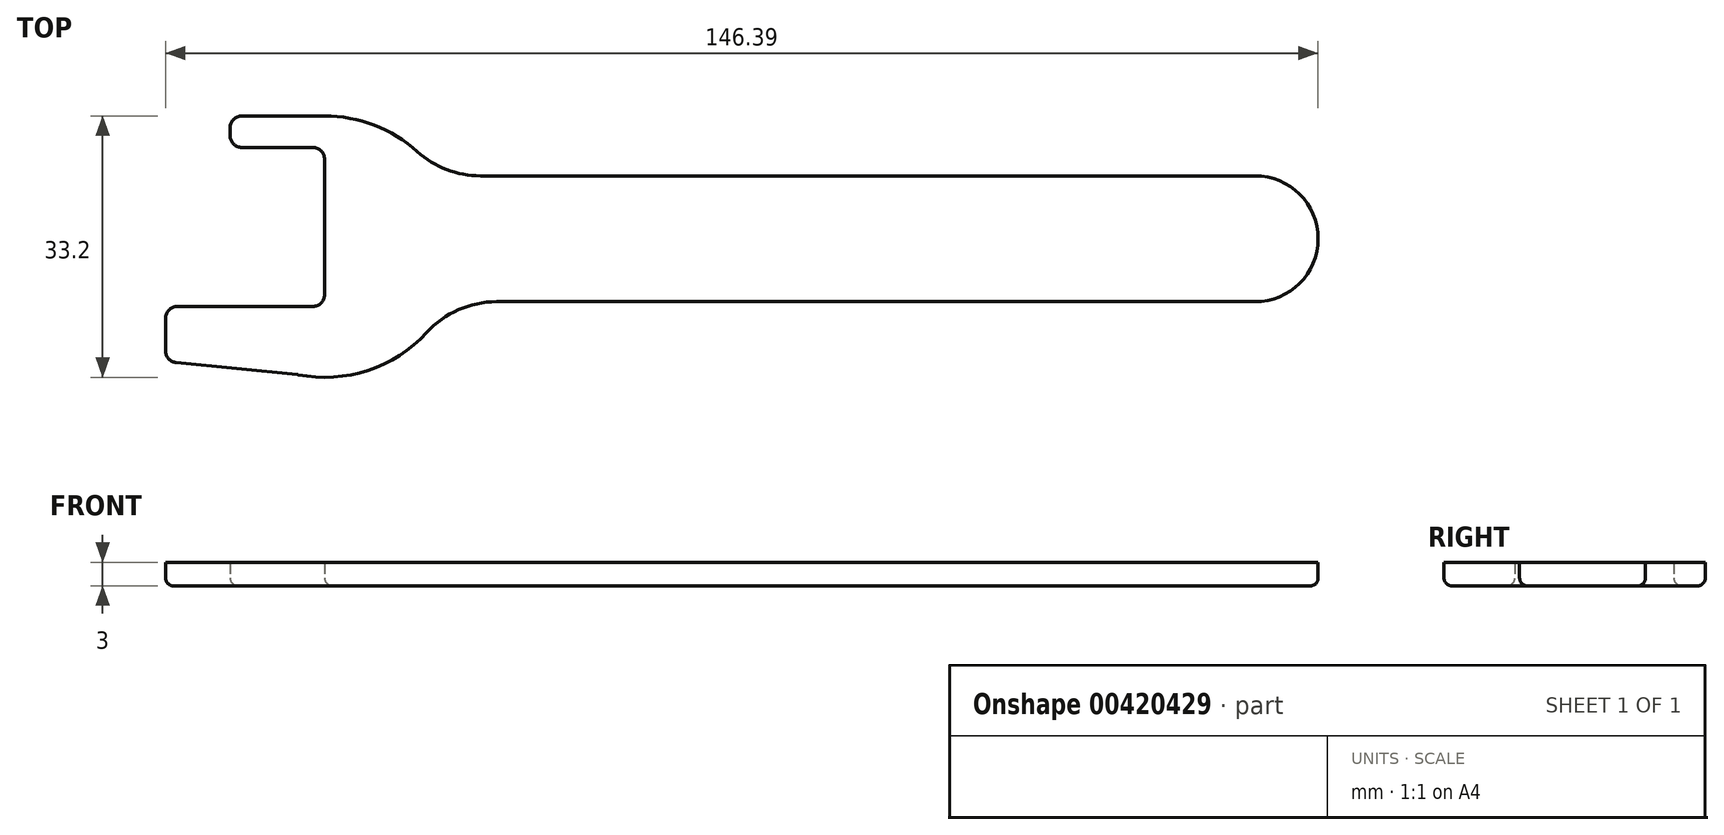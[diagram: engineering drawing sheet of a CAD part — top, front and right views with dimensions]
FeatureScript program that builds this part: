
annotation { "Feature Type Name" : "Feature", "Feature Type Description" : "" }
export const myFeature = defineFeature(function(context is Context, id is Id, definition is map)
    precondition{}
    {
        {
            var Q0;
            Q0=qCreatedBy(makeId("Top.planeOp"),FACE);
            var sketch = newSketch(context, id + "F0", { "sketchPlane" : qUnion([Q0])});
            skArc(sketch, "E0", {"start": v(-73.97, -17.26) * mm, "mid": v(-62.86, -15.84) * mm, "end": v(-54.85, -8) * mm});
            skLineSegment(sketch, "E1", {"start": v(59.4, -20.35) * mm, "end": v(59.4, 16.2) * mm, "construction": true});
            skLineSegment(sketch, "E2", {"start": v(-88.12, 35.8) * mm, "end": v(-88.12, -38.11) * mm, "construction": true});
            skLineSegment(sketch, "E3.top", {"start": v(-70.52, -17.6) * mm, "end": v(-50.32, -17.6) * mm, "construction": true});
            skLineSegment(sketch, "E3.right", {"start": v(-50.32, 17.6) * mm, "end": v(-50.32, -17.6) * mm, "construction": true});
            skLineSegment(sketch, "E4.top", {"start": v(-70.52, 11.6) * mm, "end": v(-82.52, 11.6) * mm});
            skLineSegment(sketch, "E5.top", {"start": v(-70.52, -8.6) * mm, "end": v(-90.72, -8.6) * mm});
            skLineSegment(sketch, "E5.right", {"start": v(-90.72, -15.6) * mm, "end": v(-90.72, -8.6) * mm});
            skLineSegment(sketch, "E6", {"start": v(-63.17, 15.6) * mm, "end": v(-82.52, 15.6) * mm});
            skLineSegment(sketch, "E7", {"start": v(-82.52, 15.6) * mm, "end": v(-82.52, 11.6) * mm});
            skLineSegment(sketch, "E8.trimOffspring", {"start": v(-90.72, -8.6) * mm, "end": v(-90.72, -15.6) * mm});
            skLineSegment(sketch, "E9", {"start": v(-70.52, -17.6) * mm, "end": v(-90.72, -15.6) * mm});
            skPoint(sketch, "E10.orphan", {"position": v(-90.72, -17.6) * mm});
            skLineSegment(sketch, "E11", {"start": v(-70.52, -8.6) * mm, "end": v(-70.52, 11.6) * mm});
            skLineSegment(sketch, "E12", {"start": v(-98.89, 0) * mm, "end": v(66.7, 0) * mm, "construction": true});
            skArc(sketch, "E13", {"start": v(47.67, -8) * mm, "mid": v(55.67, 0) * mm, "end": v(47.67, 8) * mm});
            skLineSegment(sketch, "E14", {"start": v(47.67, 8) * mm, "end": v(-50.32, 8) * mm});
            skLineSegment(sketch, "E15", {"start": v(47.67, -8) * mm, "end": v(-54.85, -8) * mm});
            skPoint(sketch, "E16.end.orphan", {"position": v(-61.1, 8) * mm});
            skPoint(sketch, "E17.orphan", {"position": v(-62.74, 8) * mm});
            skArc(sketch, "E18.trimOffspring", {"start": v(-56.04, 8) * mm, "mid": v(-62.35, 13.58) * mm, "end": v(-70.52, 15.6) * mm});
            skLineSegment(sketch, "E19", {"start": v(-50.32, 8) * mm, "end": v(-56.04, 8) * mm});
            skLineSegment(sketch, "E20.trimOffspring", {"start": v(-82.52, 15.6) * mm, "end": v(-46.92, 15.6) * mm, "construction": true});
            skSolve(sketch);
        }
        {
            var Q0;
            Q0=qSketchRegion(id+"F0",true);
            extrude(context, id + "F1", {"entities" : qUnion([Q0]), "depth" : 3 * mm});
        }
        {
            var Q0;
            Q0=makeQuery(id+"F1.opExtrude","SWEPT_EDGE",EDGE,{"disambiguationData":[OSD([sQuery(id+"F0.wireOp",EDGE,"E6"),sQuery(id+"F0.wireOp",EDGE,"E7")])]});
            var Q1;
            Q1=makeQuery(id+"F1.opExtrude","SWEPT_EDGE",EDGE,{"disambiguationData":[OSD([sQuery(id+"F0.wireOp",EDGE,"E4.top"),sQuery(id+"F0.wireOp",EDGE,"E7")])]});
            var Q2;
            Q2=makeQuery(id+"F1.opExtrude","SWEPT_EDGE",EDGE,{"disambiguationData":[OSD([sQuery(id+"F0.wireOp",EDGE,"E5.top"),sQuery(id+"F0.wireOp",EDGE,"E8.trimOffspring")])]});
            var Q3;
            Q3=makeQuery(id+"F1.opExtrude","SWEPT_EDGE",EDGE,{"disambiguationData":[OSD([sQuery(id+"F0.wireOp",EDGE,"E8.trimOffspring"),sQuery(id+"F0.wireOp",EDGE,"E9")])]});
            var Q4;
            Q4=makeQuery(id+"F1.opExtrude","SWEPT_EDGE",EDGE,{"disambiguationData":[OSD([sQuery(id+"F0.wireOp",EDGE,"E4.top"),sQuery(id+"F0.wireOp",EDGE,"E11")])]});
            var Q5;
            Q5=makeQuery(id+"F1.opExtrude","SWEPT_EDGE",EDGE,{"disambiguationData":[OSD([sQuery(id+"F0.wireOp",EDGE,"E5.top"),sQuery(id+"F0.wireOp",EDGE,"E11")])]});
            fillet(context, id + "F2", {"entities" : qUnion([Q0, Q1, Q2, Q3, Q4, Q5]), "radius" : 1.5 * mm, "tangentPropagation" : true, "allowEdgeOverflow" : false});
        }
        {
            var Q0;
            Q0=makeQuery(id+"F1.opExtrude","SWEPT_EDGE",EDGE,{"disambiguationData":[OSD([sQuery(id+"F0.wireOp",EDGE,"E14"),sQuery(id+"F0.wireOp",EDGE,"E18.trimOffspring")])]});
            var Q1;
            Q1=makeQuery(id+"F1.opExtrude","SWEPT_EDGE",EDGE,{"disambiguationData":[OSD([sQuery(id+"F0.wireOp",EDGE,"E0"),sQuery(id+"F0.wireOp",EDGE,"E15")])]});
            fillet(context, id + "F3", {"entities" : qUnion([Q0, Q1]), "radius" : 12 * mm, "tangentPropagation" : true, "allowEdgeOverflow" : false});
        }
        {
            var Q0;
            Q0=makeQuery(id+"F1.opExtrude","CAP_FACE",FACE,{"disambiguationData":[OSD([sQuery(id+"F0.wireOp",EDGE,"E0"),sQuery(id+"F0.wireOp",EDGE,"E4.top"),sQuery(id+"F0.wireOp",EDGE,"E5.top"),sQuery(id+"F0.wireOp",EDGE,"E6"),sQuery(id+"F0.wireOp",EDGE,"E7"),sQuery(id+"F0.wireOp",EDGE,"E8.trimOffspring"),sQuery(id+"F0.wireOp",EDGE,"E9"),sQuery(id+"F0.wireOp",EDGE,"E11"),sQuery(id+"F0.wireOp",EDGE,"E13"),sQuery(id+"F0.wireOp",EDGE,"E14"),sQuery(id+"F0.wireOp",EDGE,"E15"),sQuery(id+"F0.wireOp",EDGE,"E18.trimOffspring"),sQuery(id+"F0.wireOp",EDGE,"E19")])],"isStart":true});
            fillet(context, id + "F4", {"entities" : qUnion([Q0]), "radius" : 1 * mm, "tangentPropagation" : true, "allowEdgeOverflow" : false});
        }
    });
